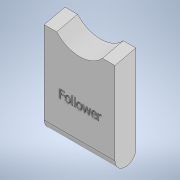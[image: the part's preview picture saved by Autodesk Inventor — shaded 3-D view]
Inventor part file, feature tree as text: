
AUTODESK INVENTOR PART (.ipt)
format: ipt  version: 2021 (Build 250183000, 183)  size: 257,024 bytes
history: native  units: mm
features: sketch x5, extrude x2, fillet x1, plane x1, sweep x1, emboss x1
ambient origin geometry x8: Origin, YZ Plane, XZ Plane, XY Plane, X Axis, Y Axis, Z Axis, Center Point
bodies: Solid1 (feature_tree)
feature tree (11):
  extrude  "Extrusion1"  Depth=23.5mm
  fillet  "Fillet2"  Radius=5.0mm
  plane  "Work Plane1"
  sweep  "Sweep1"
  extrude  "Extrusion6"  TaperAngle=0.0deg  [1 undecoded]
  emboss  "Emboss1"
  sketch  "Sketch1"  dims[d0=17.0mm d1=23.5mm d2=5.0mm d3=0.0mm]
  sketch  "Sketch5"  dims[d15=2.5mm d21=-8.5mm]
  sketch  "Sketch6"  dims[d22=2.268928mm d25=0.0mm d26=0.0mm]
  sketch  "Sketch8"  dims[d27=3.0mm]
  sketch  "Sketch9"  dims[d31=3.0mm d32=3.0mm d33=3.0mm d34=7.5mm d35=17.0mm d36=0.0mm d37=1.0mm d38=0.0mm d16=0.872665mm d17=0.5mm d18=0.872665mm]
note: 1 required parameter value undecoded (feature->parameter linkage not recoverable at this tier; creation-order binding heuristic only, values carry confidence <= 0.55)
